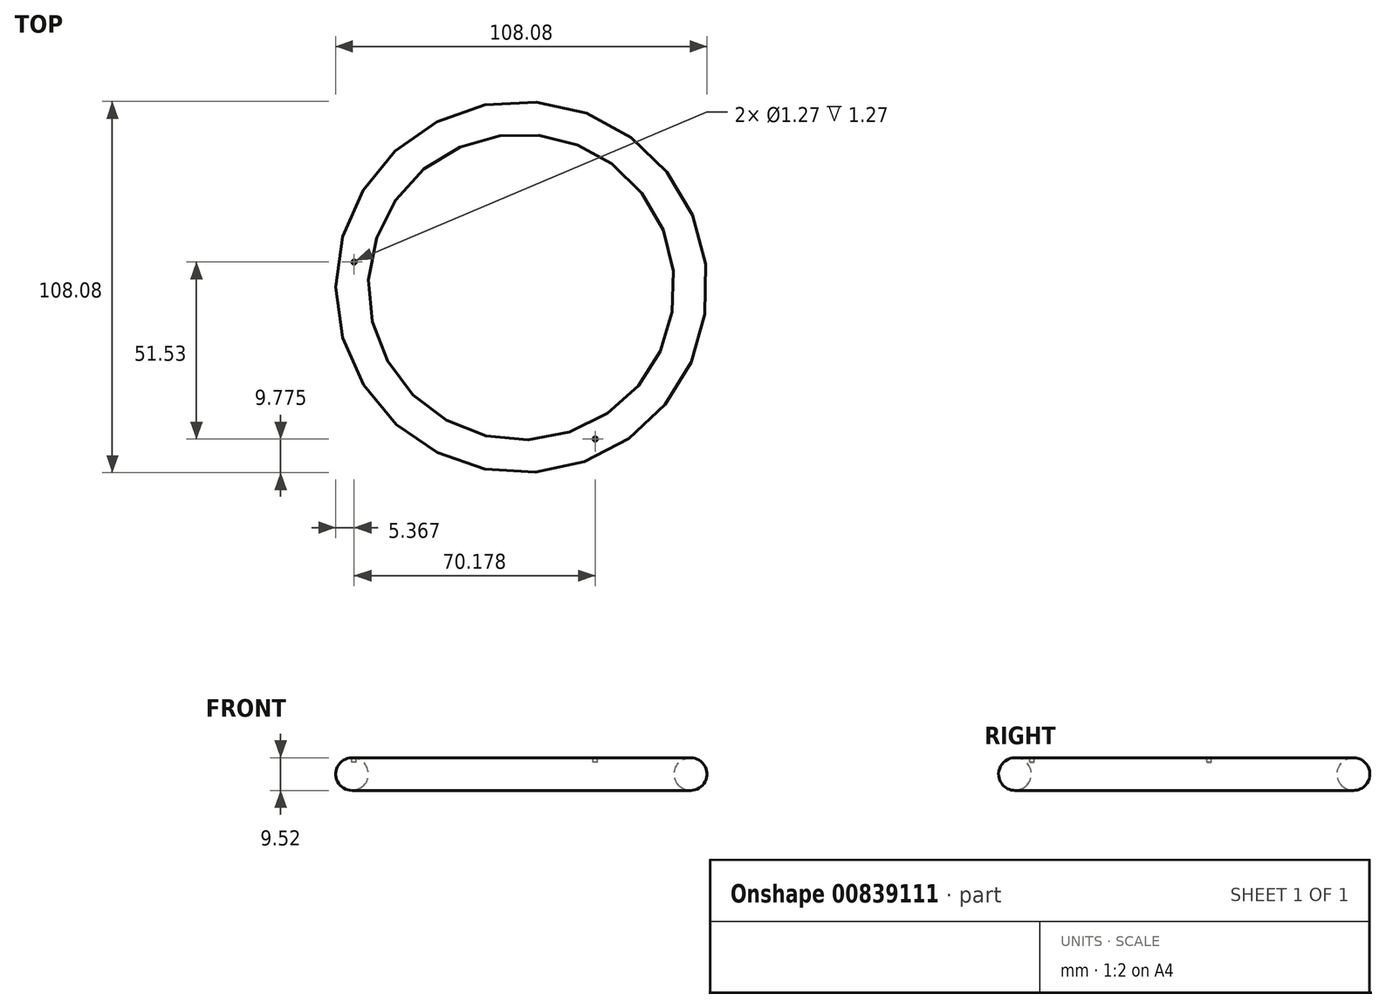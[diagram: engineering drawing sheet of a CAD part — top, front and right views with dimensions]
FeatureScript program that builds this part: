
annotation { "Feature Type Name" : "Feature", "Feature Type Description" : "" }
export const myFeature = defineFeature(function(context is Context, id is Id, definition is map)
    precondition{}
    {
        {
            var Q0;
            Q0=qCreatedBy(makeId("Front.planeOp"),FACE);
            var sketch = newSketch(context, id + "F0", { "sketchPlane" : qUnion([Q0])});
            skCircle(sketch, "E0", {"center": v(49.28, 0) * mm, "radius": 4.76 * mm});
            skLineSegment(sketch, "E1", {"start": v(0, 0) * mm, "end": v(0, 103.48) * mm, "construction": true});
            skSolve(sketch);
        }
        {
            var Q0;
            Q0 = qSketchRegion(id + "F0", true);
            var Q1;
            Q1=sQuery(id+"F0.wireOp",EDGE,"E1");
            revolve(context, id + "F1", {"surfaceOperationType" : NewSurfaceOperationType.NEW, "entities" : qUnion([Q0]), "axis" : qUnion([Q1]), "revolveType" : RevolveType.FULL});
        }
        {
            var Q0;
            Q0=qCreatedBy(makeId("Top.planeOp"),FACE);
            cPlane(context, id + "F2", {"entities" : qUnion([Q0]), "cplaneType" : CPlaneType.OFFSET, "offset" : 4.76 * mm, "width" : 152.4 * mm, "height" : 152.4 * mm});
        }
        {
            var Q0;
            Q0=qCreatedBy(id+"F2.planeOp",FACE);
            var sketch = newSketch(context, id + "F3", { "sketchPlane" : qUnion([Q0])});
            skCircle(sketch, "E2", {"center": v(0, 0) * mm, "radius": 49.21 * mm, "construction": true});
            skCircle(sketch, "E3", {"center": v(-48.67, 7.26) * mm, "radius": 0.64 * mm});
            skLineSegment(sketch, "E4", {"start": v(0, 0) * mm, "end": v(48.03, -70.14) * mm, "construction": true});
            skCircle(sketch, "E5", {"center": v(21.5, -44.27) * mm, "radius": 0.64 * mm});
            skSolve(sketch);
        }
        {
            var Q0;
            Q0=makeQuery(id+"F3.imprint","IMPRINT",FACE,{"disambiguationData":[TD([[makeQuery(id+"F3.imprint","IMPRINT",EDGE,{"derivedFrom":sQuery(id+"F3.wireOp",EDGE,"E3")}),1.0]])]});
            var Q1;
            Q1=makeQuery(id+"F3.imprint","IMPRINT",FACE,{"disambiguationData":[TD([[makeQuery(id+"F3.imprint","IMPRINT",EDGE,{"derivedFrom":sQuery(id+"F3.wireOp",EDGE,"E5")}),1.0]])]});
            extrude(context, id + "F4", {"entities" : qUnion([Q0, Q1]), "operationType" : NewBodyOperationType.REMOVE, "oppositeDirection" : true, "depth" : 1.27 * mm, "offsetDistance" : 25.4 * mm});
        }
    });
